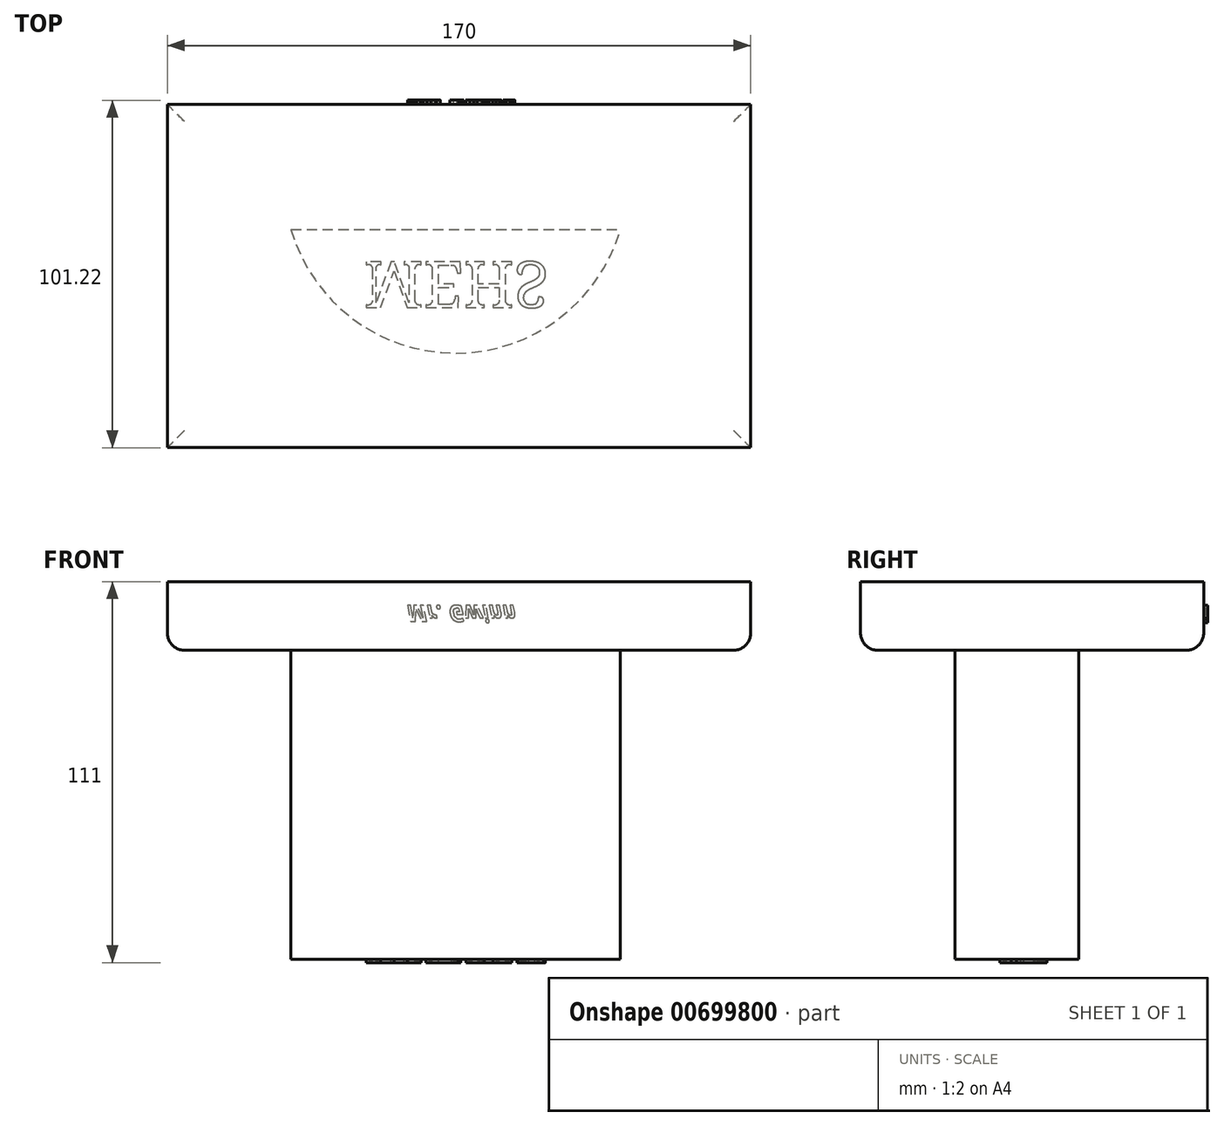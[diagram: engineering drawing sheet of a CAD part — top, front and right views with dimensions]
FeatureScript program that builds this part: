
annotation { "Feature Type Name" : "Feature", "Feature Type Description" : "" }
export const myFeature = defineFeature(function(context is Context, id is Id, definition is map)
    precondition{}
    {
        {
            var Q0;
            Q0=qCreatedBy(makeId("Top.planeOp"),FACE);
            var sketch = newSketch(context, id + "F0", { "sketchPlane" : qUnion([Q0])});
            skLineSegment(sketch, "E0.bottom", {"start": v(-84.03, 42.22) * mm, "end": v(85.97, 42.22) * mm});
            skLineSegment(sketch, "E0.top", {"start": v(-84.03, -57.78) * mm, "end": v(85.97, -57.78) * mm});
            skLineSegment(sketch, "E0.left", {"start": v(-84.03, 42.22) * mm, "end": v(-84.03, -57.78) * mm});
            skLineSegment(sketch, "E0.right", {"start": v(85.97, 42.22) * mm, "end": v(85.97, -57.78) * mm});
            skSolve(sketch);
        }
        {
            var Q0;
            Q0=makeQuery(id+"F0.imprint","IMPRINT",FACE,{"disambiguationData":[TD([[makeQuery(id+"F0.imprint","IMPRINT",EDGE,{"derivedFrom":sQuery(id+"F0.wireOp",EDGE,"E0.bottom")}),-1.0]])]});
            extrude(context, id + "F1", {"entities" : qUnion([Q0]), "oppositeDirection" : true, "depth" : 20 * mm, "offsetDistance" : 25.4 * mm});
        }
        {
            var Q0;
            Q0=makeQuery(id+"F1.opExtrude","CAP_FACE",FACE,{"disambiguationData":[OSD([sQuery(id+"F0.wireOp",EDGE,"E0.bottom"),sQuery(id+"F0.wireOp",EDGE,"E0.top"),sQuery(id+"F0.wireOp",EDGE,"E0.left"),sQuery(id+"F0.wireOp",EDGE,"E0.right")])],"isStart":false});
            var sketch = newSketch(context, id + "F2", { "sketchPlane" : qUnion([Q0])});
            skPoint(sketch, "E1", {"position": v(-50, -19.76) * mm});
            skPoint(sketch, "E2", {"position": v(50, -19.76) * mm});
            skLineSegment(sketch, "E3", {"start": v(-48, -5.76) * mm, "end": v(48, -5.76) * mm});
            skArc(sketch, "E4", {"start": v(48, -5.76) * mm, "mid": v(0, 30.24) * mm, "end": v(-48, -5.76) * mm});
            skSolve(sketch);
        }
        {
            var Q0;
            Q0 = qSketchRegion(id + "F2", true);
            extrude(context, id + "F3", {"entities" : qUnion([Q0]), "operationType" : NewBodyOperationType.ADD, "depth" : 90 * mm, "offsetDistance" : 25 * mm});
        }
        {
            var Q0;
            Q0=makeQuery(id+"F1.opExtrude","SWEPT_FACE",FACE,{"disambiguationData":[OSD([sQuery(id+"F0.wireOp",EDGE,"E0.bottom")])]});
            var sketch = newSketch(context, id + "F4", { "sketchPlane" : qUnion([Q0])});
            skText(sketch, "E5", { "text": "Mr. Gwinn ", "fontName": "NotoSans-BoldItalic.ttf"});
            const initialGuessF4  = {"E5": [0.01424, -0.00695, -1, 0, 0.00475]};
            skSetInitialGuess(sketch, initialGuessF4);
            skSolve(sketch);
        }
        {
            var Q0;
            Q0 = qSketchRegion(id + "F4", true);
            extrude(context, id + "F5", {"entities" : qUnion([Q0]), "operationType" : NewBodyOperationType.ADD, "depth" : 1.22 * mm, "offsetDistance" : 25 * mm});
        }
        {
            var Q0;
            {var subQ1=sQuery(id+"F0.wireOp",EDGE,"E0.left");var subQ2=sQuery(id+"F0.wireOp",EDGE,"E0.bottom");var subQ3=makeQuery(id+"F1.opExtrude","CAP_FACE",FACE,{"disambiguationData":[OSD([subQ2,sQuery(id+"F0.wireOp",EDGE,"E0.top"),subQ1,sQuery(id+"F0.wireOp",EDGE,"E0.right")])],"isStart":false});var subQ4=makeQuery(id+"F1.opExtrude","SWEPT_FACE",FACE,{"disambiguationData":[OSD([subQ2])]});Q0=makeQuery(id+"F5.boolean.opBoolean","SPLIT",EDGE,{"disambiguationData":[topologyDisambiguationEdgeConnected([subQ4,subQ3]),TD([makeQuery(id+"F1.opExtrude","SWEPT_FACE",FACE,{"disambiguationData":[OSD([subQ1])]})])],"derivedFrom":makeQuery(id+"F1.opExtrude","CAP_EDGE",EDGE,{"disambiguationData":[OSD([subQ2])],"isStart":false})});}
            var Q1;
            Q1=makeQuery(id+"F1.opExtrude","CAP_EDGE",EDGE,{"disambiguationData":[OSD([sQuery(id+"F0.wireOp",EDGE,"E0.left")])],"isStart":false});
            var Q2;
            Q2=makeQuery(id+"F1.opExtrude","CAP_EDGE",EDGE,{"disambiguationData":[OSD([sQuery(id+"F0.wireOp",EDGE,"E0.right")])],"isStart":false});
            var Q3;
            {var subQ1=sQuery(id+"F0.wireOp",EDGE,"E0.right");var subQ2=sQuery(id+"F0.wireOp",EDGE,"E0.bottom");var subQ3=makeQuery(id+"F1.opExtrude","CAP_FACE",FACE,{"disambiguationData":[OSD([subQ2,sQuery(id+"F0.wireOp",EDGE,"E0.top"),sQuery(id+"F0.wireOp",EDGE,"E0.left"),subQ1])],"isStart":false});var subQ4=makeQuery(id+"F1.opExtrude","SWEPT_FACE",FACE,{"disambiguationData":[OSD([subQ2])]});Q3=makeQuery(id+"F5.boolean.opBoolean","SPLIT",EDGE,{"disambiguationData":[topologyDisambiguationEdgeConnected([subQ4,subQ3]),TD([makeQuery(id+"F1.opExtrude","SWEPT_FACE",FACE,{"disambiguationData":[OSD([subQ1])]})])],"derivedFrom":makeQuery(id+"F1.opExtrude","CAP_EDGE",EDGE,{"disambiguationData":[OSD([subQ2])],"isStart":false})});}
            var Q4;
            Q4=makeQuery(id+"F1.opExtrude","CAP_EDGE",EDGE,{"disambiguationData":[OSD([sQuery(id+"F0.wireOp",EDGE,"E0.top")])],"isStart":false});
            fillet(context, id + "F6", {"entities" : qUnion([Q0, Q1, Q2, Q3, Q4]), "radius" : 5 * mm, "tangentPropagation" : true, "allowEdgeOverflow" : false});
        }
        {
            var Q0;
            Q0=makeQuery(id+"F3.opExtrude","CAP_FACE",FACE,{"disambiguationData":[OSD([sQuery(id+"F2.wireOp",EDGE,"E3"),sQuery(id+"F2.wireOp",EDGE,"E4")])],"isStart":false});
            var sketch = newSketch(context, id + "F7", { "sketchPlane" : qUnion([Q0])});
            skText(sketch, "E6", { "text": "MEHS", "fontName": "NotoSerif-Regular.ttf"});
            const initialGuessF7  = {"E6": [-0.02678, 0.00366, 1, 0, 0.01339]};
            skSetInitialGuess(sketch, initialGuessF7);
            skSolve(sketch);
        }
        {
            var Q0;
            Q0 = qSketchRegion(id + "F7", true);
            extrude(context, id + "F8", {"entities" : qUnion([Q0]), "operationType" : NewBodyOperationType.ADD, "depth" : 1 * mm, "offsetDistance" : 25 * mm});
        }
    });
